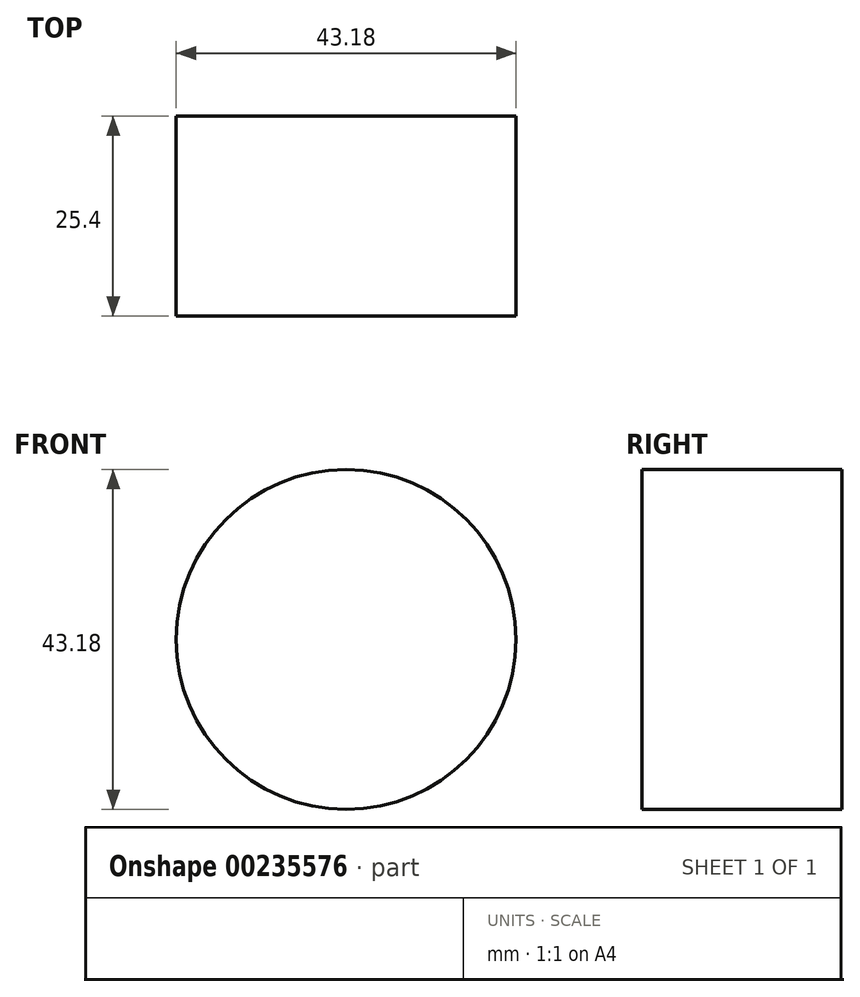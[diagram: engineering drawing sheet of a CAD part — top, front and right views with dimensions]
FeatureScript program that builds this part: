
annotation { "Feature Type Name" : "Feature", "Feature Type Description" : "" }
export const myFeature = defineFeature(function(context is Context, id is Id, definition is map)
    precondition{}
    {
        {
            var Q0;
            Q0=qCreatedBy(makeId("Front.planeOp"),FACE);
            var sketch = newSketch(context, id + "F0", { "sketchPlane" : qUnion([Q0])});
            skCircle(sketch, "E0", {"center": v(-8.2, 0) * mm, "radius": 25.4 * mm});
            skCircle(sketch, "E1", {"center": v(-8.2, 0) * mm, "radius": 21.59 * mm});
            skSolve(sketch);
        }
        {
            var Q0;
            Q0=makeQuery(id+"F0.imprint","IMPRINT",FACE,{"disambiguationData":[TD([[makeQuery(id+"F0.imprint","IMPRINT",EDGE,{"derivedFrom":sQuery(id+"F0.wireOp",EDGE,"E1")}),1.0]])]});
            extrude(context, id + "F1", {"entities" : qUnion([Q0]), "depth" : 25.4 * mm});
        }
    });
